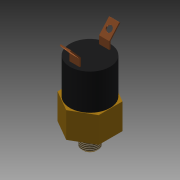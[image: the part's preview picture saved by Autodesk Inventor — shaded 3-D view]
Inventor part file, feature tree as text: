
AUTODESK INVENTOR PART (.ipt)
format: ipt  version: 2016 SP1 (Build 200210100, 210)  size: 161,792 bytes
history: native  units: mm (DEFAULTED — no unit token found)
features: extrude x6, sketch x6, projected_geometry x4, mirror x1, thread x1, chamfer x1, fillet x1
ambient origin geometry x8: Origin, YZ Plane, XZ Plane, XY Plane, X Axis, Y Axis, Z Axis, Center Point
bodies: Solid1 (feature_tree)
feature tree (20):
  extrude  "Extrusion1"  Depth=15.875mm TaperAngle=0.0deg
  extrude  "Extrusion2"  Depth=11.049mm TaperAngle=0.0deg
  extrude  "Extrusion3"  Depth=19.9898mm TaperAngle=0.0deg
  extrude  "Extrusion4"  Depth=21.971mm TaperAngle=0.0deg
  extrude  "Extrusion5"  Depth=0.762mm
  extrude  "Extrusion6"  Depth=3.175mm
  mirror  "Mirror1"
  thread  "Thread1"  [1 undecoded]
  chamfer  "Chamfer1"  Distance=6.35mm
  fillet  "Fillet1"  Radius=6.35mm
  sketch  "Sketch1"  dims[d0=25.4mm d1=15.875mm d2=0.0mm]
  sketch  "Sketch2"  dims[d3=10.16mm d4=11.049mm d5=0.0mm]
  projected_geometry  "Projected Loop1"
  sketch  "Sketch3"  dims[d6=3.175mm d7=19.9898mm d8=0.0mm]
  sketch  "Sketch4"  dims[d9=24.765mm d10=21.971mm d11=0.0mm]
  projected_geometry  "Projected Loop2"
  sketch  "Sketch5"  dims[d12=19.05mm d13=0.762mm]
  projected_geometry  "Projected Loop3"
  sketch  "Sketch6"  dims[d14=0.762mm d15=4.699mm d17=9.398mm d18=6.35mm d19=0.0mm d20=6.35mm d21=0.0mm d22=25.4mm d23=0.0mm d24=1.0mm d25=3.175mm d26=45.0deg d27=3.175mm]
  projected_geometry  "Projected Loop4"
note: 1 required parameter value undecoded (feature->parameter linkage not recoverable at this tier; creation-order binding heuristic only, values carry confidence <= 0.55)
